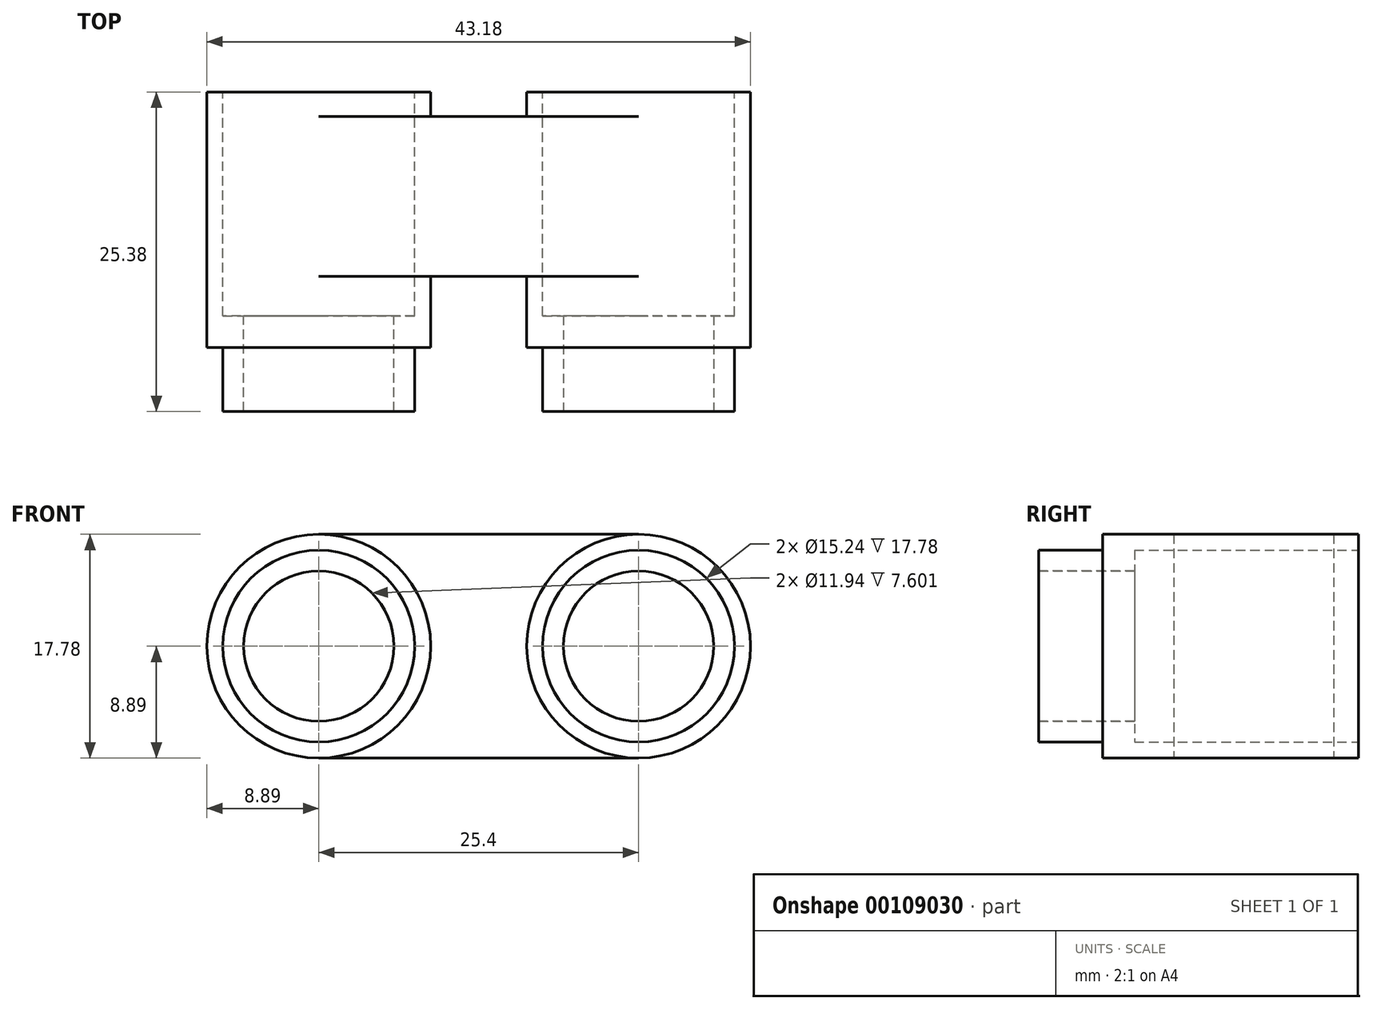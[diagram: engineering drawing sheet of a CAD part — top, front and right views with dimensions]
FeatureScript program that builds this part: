
annotation { "Feature Type Name" : "Feature", "Feature Type Description" : "" }
export const myFeature = defineFeature(function(context is Context, id is Id, definition is map)
    precondition{}
    {
        {
            var Q0;
            Q0=qCreatedBy(makeId("Top.planeOp"),FACE);
            var sketch = newSketch(context, id + "F0", { "sketchPlane" : qUnion([Q0])});
            skLineSegment(sketch, "E0", {"start": v(0, 0) * mm, "end": v(25.4, 0) * mm});
            skLineSegment(sketch, "E1", {"start": v(0, 0) * mm, "end": v(0, 35.92) * mm});
            skLineSegment(sketch, "E2", {"start": v(25.4, 0) * mm, "end": v(25.4, 35.92) * mm});
            skArc(sketch, "E3", {"start": v(0, 35.92) * mm, "mid": v(12.7, 48.62) * mm, "end": v(25.4, 35.92) * mm});
            skLineSegment(sketch, "E4", {"start": v(12.7, 48.62) * mm, "end": v(12.7, 20.3) * mm});
            skLineSegment(sketch, "E5", {"start": v(12.7, 20.3) * mm, "end": v(-12.3, 20.3) * mm});
            skLineSegment(sketch, "E6", {"start": v(-12.3, 20.3) * mm, "end": v(-12.3, 60.97) * mm});
            skLineSegment(sketch, "E7", {"start": v(-12.3, 60.97) * mm, "end": v(40.22, 60.97) * mm});
            skLineSegment(sketch, "E8", {"start": v(40.22, 60.97) * mm, "end": v(40.22, 20.3) * mm});
            skLineSegment(sketch, "E9", {"start": v(12.7, 20.3) * mm, "end": v(40.22, 20.3) * mm});
            skLineSegment(sketch, "E10", {"start": v(0, 18.35) * mm, "end": v(25.4, 18.35) * mm});
            skLineSegment(sketch, "E11", {"start": v(0, 5.65) * mm, "end": v(25.4, 5.65) * mm});
            skSolve(sketch);
        }
        {
            var Q0;
            Q0=qCreatedBy(makeId("Front.planeOp"),FACE);
            var sketch = newSketch(context, id + "F1", { "sketchPlane" : qUnion([Q0])});
            skCircle(sketch, "E12", {"center": v(0, 0) * mm, "radius": 5.97 * mm});
            skCircle(sketch, "E13", {"center": v(0, 0) * mm, "radius": 8.9 * mm});
            skSolve(sketch);
        }
        {
            var Q0;
            Q0=makeQuery(id+"F1.imprint","IMPRINT",FACE,{"disambiguationData":[TD([[makeQuery(id+"F1.imprint","IMPRINT",EDGE,{"derivedFrom":sQuery(id+"F1.wireOp",EDGE,"E12")}),-1.0]])]});
            var Q1;
            Q1=sQuery(id+"F0.wireOp",EDGE,"E1");
            var Q2;
            Q2=sQuery(id+"F0.wireOp",EDGE,"E3");
            var Q3;
            Q3=sQuery(id+"F0.wireOp",EDGE,"E2");
            sweep(context, id + "F2", {"profiles" : qUnion([Q0]), "path" : qUnion([Q1, Q2, Q3])});
        }
        {
            var Q0;
            Q0=makeQuery(id+"F2.opSweep","CAP_FACE",FACE,{"disambiguationData":[OSD([sQuery(id+"F0.wireOp",VERTEX,"E1.start"),sQuery(id+"F1.wireOp",EDGE,"E12"),sQuery(id+"F1.wireOp",EDGE,"E13")])],"isStart":true});
            var sketch = newSketch(context, id + "F3", { "sketchPlane" : qUnion([Q0])});
            skCircle(sketch, "E14", {"center": v(0, 0) * mm, "radius": 7.62 * mm});
            skCircle(sketch, "E15", {"center": v(25.4, 0) * mm, "radius": 7.62 * mm});
            skLineSegment(sketch, "E16", {"start": v(0, 0) * mm, "end": v(25.4, 0) * mm});
            skCircle(sketch, "E17", {"center": v(25.4, 0) * mm, "radius": 8.9 * mm});
            skSolve(sketch);
        }
        {
            var Q0;
            Q0=makeQuery(id+"F2.opSweep","CAP_FACE",FACE,{"disambiguationData":[OSD([sQuery(id+"F0.wireOp",VERTEX,"E2.start"),sQuery(id+"F1.wireOp",EDGE,"E12"),sQuery(id+"F1.wireOp",EDGE,"E13")])],"isStart":false});
            var sketch = newSketch(context, id + "F4", { "sketchPlane" : qUnion([Q0])});
            skCircle(sketch, "E18", {"center": v(25.4, 0) * mm, "radius": 7.62 * mm});
            skSolve(sketch);
        }
        {
            var Q0;
            Q0=makeQuery(id+"F3.imprint","IMPRINT",FACE,{"disambiguationData":[TD([[makeQuery(id+"F3.imprint","IMPRINT",EDGE,{"derivedFrom":sQuery(id+"F3.wireOp",EDGE,"E14")}),1.0]])]});
            var Q1;
            Q1=makeQuery(id+"F4.imprint","IMPRINT",FACE,{"disambiguationData":[TD([[makeQuery(id+"F4.imprint","IMPRINT",EDGE,{"derivedFrom":sQuery(id+"F4.wireOp",EDGE,"E18")}),1.0]])]});
            extrude(context, id + "F5", {"entities" : qUnion([Q0, Q1]), "operationType" : NewBodyOperationType.ADD, "depth" : 5.08 * mm});
        }
        {
            var Q0;
            {var subQ11=sQuery(id+"F0.wireOp",EDGE,"E6");Q0=makeQuery(id+"F0.imprint","IMPRINT",FACE,{"disambiguationData":[TD([[makeQuery(id+"F0.imprint","IMPRINT",EDGE,{"derivedFrom":subQ11}),-1.0]])]});}
            var Q1;
            {var subQ5=sQuery(id+"F0.wireOp",EDGE,"E4");Q1=makeQuery(id+"F0.imprint","IMPRINT",FACE,{"disambiguationData":[TD([[makeQuery(id+"F0.imprint","IMPRINT",EDGE,{"derivedFrom":subQ5}),-1.0]])]});}
            var Q2;
            {var subQ5=sQuery(id+"F0.wireOp",EDGE,"E4");Q2=makeQuery(id+"F0.imprint","IMPRINT",FACE,{"disambiguationData":[TD([[makeQuery(id+"F0.imprint","IMPRINT",EDGE,{"derivedFrom":subQ5}),1.0]])]});}
            extrude(context, id + "F6", {"entities" : qUnion([Q0, Q1, Q2]), "operationType" : NewBodyOperationType.REMOVE, "oppositeDirection" : true, "depth" : 25.4 * mm, "hasSecondDirection" : true, "secondDirectionOppositeDirection" : false, "secondDirectionDepth" : 25.4 * mm});
        }
        {
            var Q0;
            Q0=makeQuery(id+"F6.boolean.opBoolean","COPY",FACE,{"disambiguationData":[OD(1.0)],"derivedFrom":makeQuery(id+"F6.opExtrude","SWEPT_FACE",FACE,{"disambiguationData":[OSD([sQuery(id+"F0.wireOp",EDGE,"E5"),sQuery(id+"F0.wireOp",EDGE,"E9")])]})});
            var sketch = newSketch(context, id + "F7", { "sketchPlane" : qUnion([Q0])});
            skCircle(sketch, "E19", {"center": v(-25.4, 0) * mm, "radius": 7.62 * mm});
            skSolve(sketch);
        }
        {
            var Q0;
            Q0=makeQuery(id+"F6.boolean.opBoolean","COPY",FACE,{"disambiguationData":[OD(0.0)],"derivedFrom":makeQuery(id+"F6.opExtrude","SWEPT_FACE",FACE,{"disambiguationData":[OSD([sQuery(id+"F0.wireOp",EDGE,"E5"),sQuery(id+"F0.wireOp",EDGE,"E9")])]})});
            var sketch = newSketch(context, id + "F8", { "sketchPlane" : qUnion([Q0])});
            skCircle(sketch, "E20", {"center": v(0, 0) * mm, "radius": 7.62 * mm});
            skSolve(sketch);
        }
        {
            var Q0;
            Q0=makeQuery(id+"F7.imprint","IMPRINT",FACE,{"disambiguationData":[TD([[makeQuery(id+"F7.imprint","IMPRINT",EDGE,{"derivedFrom":sQuery(id+"F7.wireOp",EDGE,"E19")}),1.0]])]});
            var Q1;
            Q1=makeQuery(id+"F8.imprint","IMPRINT",FACE,{"disambiguationData":[TD([[makeQuery(id+"F8.imprint","IMPRINT",EDGE,{"derivedFrom":sQuery(id+"F8.wireOp",EDGE,"E20")}),1.0]])]});
            extrude(context, id + "F9", {"entities" : qUnion([Q0, Q1]), "operationType" : NewBodyOperationType.REMOVE, "oppositeDirection" : true, "depth" : 17.78 * mm});
        }
        {
            var Q0;
            {var subQ0=sQuery(id+"F0.wireOp",EDGE,"E10");Q0=makeQuery(id+"F0.imprint","IMPRINT",FACE,{"disambiguationData":[TD([[makeQuery(id+"F0.imprint","IMPRINT",EDGE,{"derivedFrom":subQ0}),-1.0]])]});}
            extrude(context, id + "F10", {"entities" : qUnion([Q0]), "operationType" : NewBodyOperationType.ADD, "depth" : 8.9 * mm, "hasSecondDirection" : true, "secondDirectionOppositeDirection" : true, "secondDirectionDepth" : 8.9 * mm});
        }
        {
            var Q0;
            Q0 = qSketchRegion(id + "F7", true);
            var Q1;
            Q1 = qSketchRegion(id + "F8", true);
            extrude(context, id + "F11", {"entities" : qUnion([Q0, Q1]), "operationType" : NewBodyOperationType.REMOVE, "oppositeDirection" : true, "depth" : 17.78 * mm});
        }
        {
            var Q0;
            {var subQ0=sQuery(id+"F1.wireOp",EDGE,"E12");Q0=makeQuery(id+"F8.imprint","IMPRINT",FACE,{"disambiguationData":[TD([[makeQuery(id+"F8.imprint","IMPRINT",EDGE,{"derivedFrom":makeQuery(id+"F6.boolean.opBoolean","INTERSECT",EDGE,{"derivedFrom":[makeQuery(id+"F5.boolean.opBoolean","MERGE",FACE,{"derivedFrom":[makeQuery(id+"F2.opSweep","SWEPT_FACE",FACE,{"disambiguationData":[OSD([sQuery(id+"F0.wireOp",EDGE,"E1"),subQ0])]}),makeQuery(id+"F5.opExtrude","SWEPT_FACE",FACE,{"disambiguationData":[OSD([sQuery(id+"F0.wireOp",VERTEX,"E1.start"),subQ0])]})]}),makeQuery(id+"F6.opExtrude","SWEPT_FACE",FACE,{"disambiguationData":[OSD([sQuery(id+"F0.wireOp",EDGE,"E5"),sQuery(id+"F0.wireOp",EDGE,"E9")])]})]})}),1.0]])]});}
            var Q1;
            {var subQ0=sQuery(id+"F1.wireOp",EDGE,"E12");Q1=makeQuery(id+"F7.imprint","IMPRINT",FACE,{"disambiguationData":[TD([[makeQuery(id+"F7.imprint","IMPRINT",EDGE,{"derivedFrom":makeQuery(id+"F6.boolean.opBoolean","INTERSECT",EDGE,{"derivedFrom":[makeQuery(id+"F5.boolean.opBoolean","MERGE",FACE,{"derivedFrom":[makeQuery(id+"F2.opSweep","SWEPT_FACE",FACE,{"disambiguationData":[OSD([sQuery(id+"F0.wireOp",EDGE,"E2"),subQ0])]}),makeQuery(id+"F5.opExtrude","SWEPT_FACE",FACE,{"disambiguationData":[OSD([sQuery(id+"F0.wireOp",VERTEX,"E2.start"),subQ0])]})]}),makeQuery(id+"F6.opExtrude","SWEPT_FACE",FACE,{"disambiguationData":[OSD([sQuery(id+"F0.wireOp",EDGE,"E5"),sQuery(id+"F0.wireOp",EDGE,"E9")])]})]})}),1.0]])]});}
            extrude(context, id + "F12", {"entities" : qUnion([Q0, Q1]), "operationType" : NewBodyOperationType.REMOVE, "oppositeDirection" : true, "depth" : 25.4 * mm});
        }
    });
